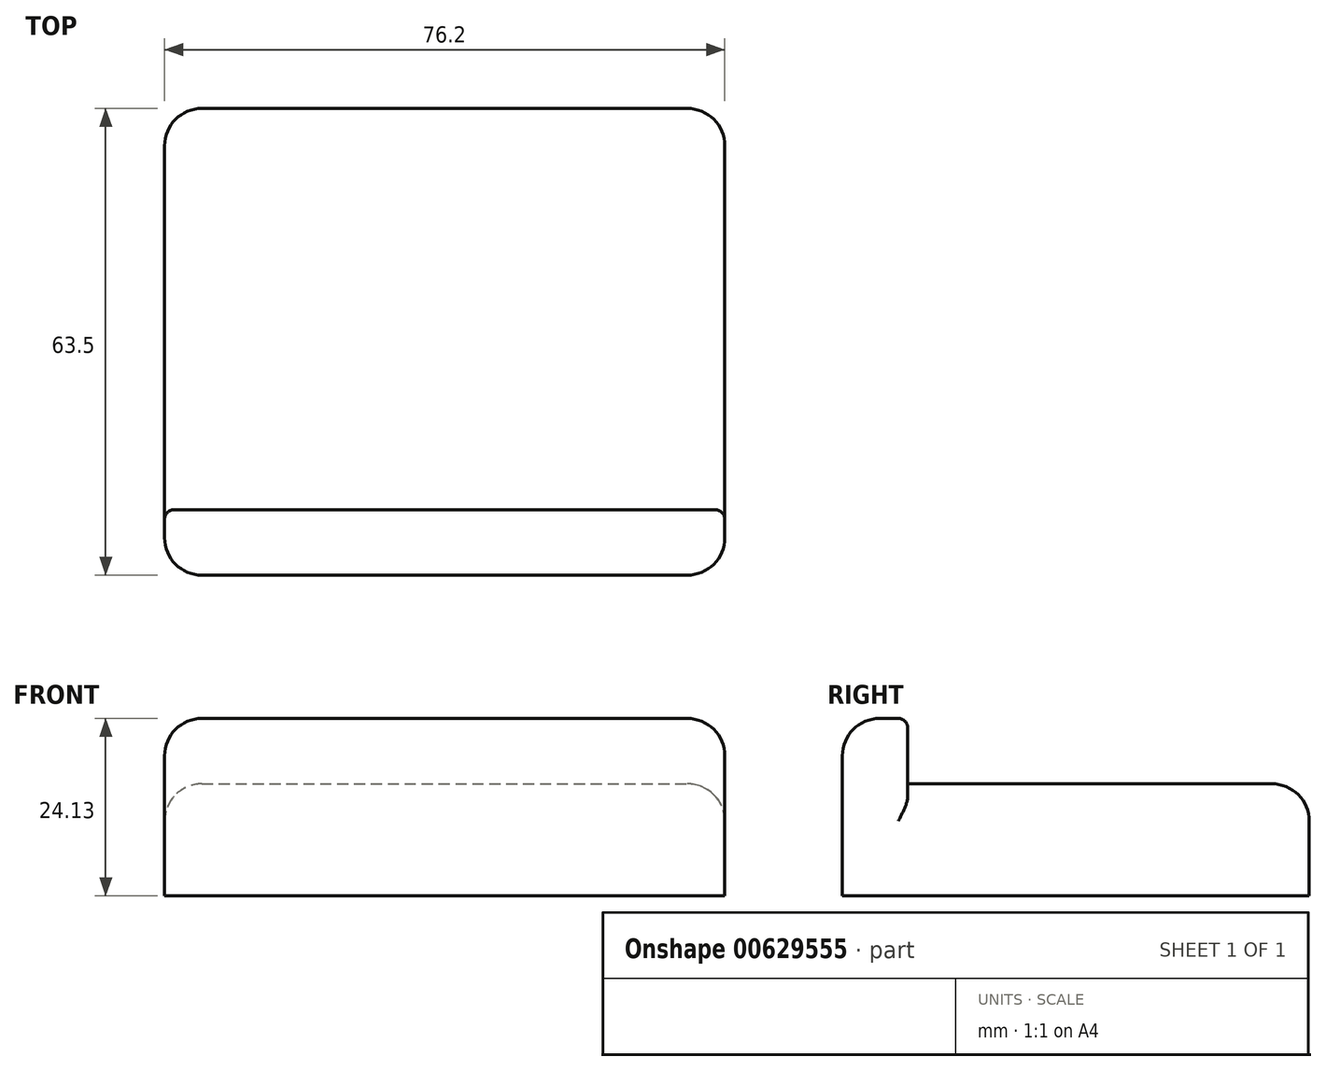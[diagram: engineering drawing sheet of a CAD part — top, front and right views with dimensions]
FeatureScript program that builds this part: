
annotation { "Feature Type Name" : "Feature", "Feature Type Description" : "" }
export const myFeature = defineFeature(function(context is Context, id is Id, definition is map)
    precondition{}
    {
        {
            var Q0;
            Q0=qCreatedBy(makeId("Top.planeOp"),FACE);
            var sketch = newSketch(context, id + "F0", { "sketchPlane" : qUnion([Q0])});
            skLineSegment(sketch, "E0.bottom", {"start": v(38.1, 31.75) * mm, "end": v(-38.1, 31.75) * mm});
            skLineSegment(sketch, "E0.top", {"start": v(38.1, -31.75) * mm, "end": v(-38.1, -31.75) * mm});
            skLineSegment(sketch, "E0.left", {"start": v(38.1, 31.75) * mm, "end": v(38.1, -31.75) * mm});
            skLineSegment(sketch, "E0.right", {"start": v(-38.1, 31.75) * mm, "end": v(-38.1, -31.75) * mm});
            skPoint(sketch, "E0.middle", {"position": v(0, 0) * mm});
            skSolve(sketch);
        }
        {
            var Q0;
            Q0 = qSketchRegion(id + "F0", true);
            extrude(context, id + "F1", {"entities" : qUnion([Q0]), "depth" : 15.24 * mm, "offsetDistance" : 25.4 * mm});
        }
        {
            var Q0;
            Q0=makeQuery(id+"F1.opExtrude","CAP_FACE",FACE,{"disambiguationData":[OSD([sQuery(id+"F0.wireOp",EDGE,"E0.bottom"),sQuery(id+"F0.wireOp",EDGE,"E0.top"),sQuery(id+"F0.wireOp",EDGE,"E0.left"),sQuery(id+"F0.wireOp",EDGE,"E0.right")])],"isStart":false});
            var sketch = newSketch(context, id + "F2", { "sketchPlane" : qUnion([Q0])});
            skLineSegment(sketch, "E1.bottom", {"start": v(-38.1, -31.75) * mm, "end": v(38.1, -31.75) * mm});
            skLineSegment(sketch, "E1.top", {"start": v(-38.1, -22.86) * mm, "end": v(38.1, -22.86) * mm});
            skLineSegment(sketch, "E1.left", {"start": v(-38.1, -31.75) * mm, "end": v(-38.1, -22.86) * mm});
            skLineSegment(sketch, "E1.right", {"start": v(38.1, -31.75) * mm, "end": v(38.1, -22.86) * mm});
            skSolve(sketch);
        }
        {
            var Q0;
            Q0 = qSketchRegion(id + "F2", true);
            extrude(context, id + "F3", {"entities" : qUnion([Q0]), "operationType" : NewBodyOperationType.ADD, "depth" : 8.9 * mm, "offsetDistance" : 25.4 * mm});
        }
        {
            var Q0;
            Q0=makeQuery(id+"F3.boolean.opBoolean","MERGE",EDGE,{"derivedFrom":[makeQuery(id+"F1.opExtrude","SWEPT_EDGE",EDGE,{"disambiguationData":[OSD([sQuery(id+"F0.wireOp",EDGE,"E0.top"),sQuery(id+"F0.wireOp",EDGE,"E0.left")])]}),makeQuery(id+"F3.opExtrude","SWEPT_EDGE",EDGE,{"disambiguationData":[OSD([sQuery(id+"F2.wireOp",EDGE,"E1.bottom"),sQuery(id+"F2.wireOp",EDGE,"E1.right")])]})]});
            var Q1;
            Q1=makeQuery(id+"F3.boolean.opBoolean","MERGE",EDGE,{"derivedFrom":[makeQuery(id+"F1.opExtrude","SWEPT_EDGE",EDGE,{"disambiguationData":[OSD([sQuery(id+"F0.wireOp",EDGE,"E0.top"),sQuery(id+"F0.wireOp",EDGE,"E0.right")])]}),makeQuery(id+"F3.opExtrude","SWEPT_EDGE",EDGE,{"disambiguationData":[OSD([sQuery(id+"F2.wireOp",EDGE,"E1.bottom"),sQuery(id+"F2.wireOp",EDGE,"E1.left")])]})]});
            var Q2;
            Q2=makeQuery(id+"F3.opExtrude","CAP_EDGE",EDGE,{"disambiguationData":[OSD([sQuery(id+"F2.wireOp",EDGE,"E1.bottom")])],"isStart":false});
            fillet(context, id + "F4", {"entities" : qUnion([Q0, Q1, Q2]), "radius" : 5.08 * mm, "tangentPropagation" : true, "allowEdgeOverflow" : false});
        }
        {
            var Q0;
            Q0=makeQuery(id+"F3.opExtrude","CAP_EDGE",EDGE,{"disambiguationData":[OSD([sQuery(id+"F2.wireOp",EDGE,"E1.left")])],"isStart":false});
            var Q1;
            Q1=makeQuery(id+"F3.opExtrude","CAP_EDGE",EDGE,{"disambiguationData":[OSD([sQuery(id+"F2.wireOp",EDGE,"E1.right")])],"isStart":false});
            var Q2;
            Q2=makeQuery(id+"F1.opExtrude","CAP_EDGE",EDGE,{"disambiguationData":[OSD([sQuery(id+"F0.wireOp",EDGE,"E0.right")])],"isStart":false});
            var Q3;
            Q3=makeQuery(id+"F1.opExtrude","CAP_EDGE",EDGE,{"disambiguationData":[OSD([sQuery(id+"F0.wireOp",EDGE,"E0.bottom")])],"isStart":false});
            var Q4;
            Q4=makeQuery(id+"F1.opExtrude","CAP_EDGE",EDGE,{"disambiguationData":[OSD([sQuery(id+"F0.wireOp",EDGE,"E0.left")])],"isStart":false});
            var Q5;
            Q5=makeQuery(id+"F1.opExtrude","SWEPT_EDGE",EDGE,{"disambiguationData":[OSD([sQuery(id+"F0.wireOp",EDGE,"E0.bottom"),sQuery(id+"F0.wireOp",EDGE,"E0.left")])]});
            var Q6;
            Q6=makeQuery(id+"F1.opExtrude","SWEPT_EDGE",EDGE,{"disambiguationData":[OSD([sQuery(id+"F0.wireOp",EDGE,"E0.bottom"),sQuery(id+"F0.wireOp",EDGE,"E0.right")])]});
            fillet(context, id + "F5", {"entities" : qUnion([Q0, Q1, Q2, Q3, Q4, Q5, Q6]), "radius" : 5.08 * mm, "tangentPropagation" : true, "allowEdgeOverflow" : false});
        }
        {
            var Q0;
            Q0=makeQuery(id+"F3.opExtrude","SWEPT_EDGE",EDGE,{"disambiguationData":[OSD([sQuery(id+"F0.wireOp",EDGE,"E0.right"),sQuery(id+"F2.wireOp",EDGE,"E1.top"),sQuery(id+"F2.wireOp",EDGE,"E1.left")])]});
            fillet(context, id + "F6", {"entities" : qUnion([Q0]), "radius" : 1.27 * mm, "tangentPropagation" : true, "allowEdgeOverflow" : false});
        }
    });
